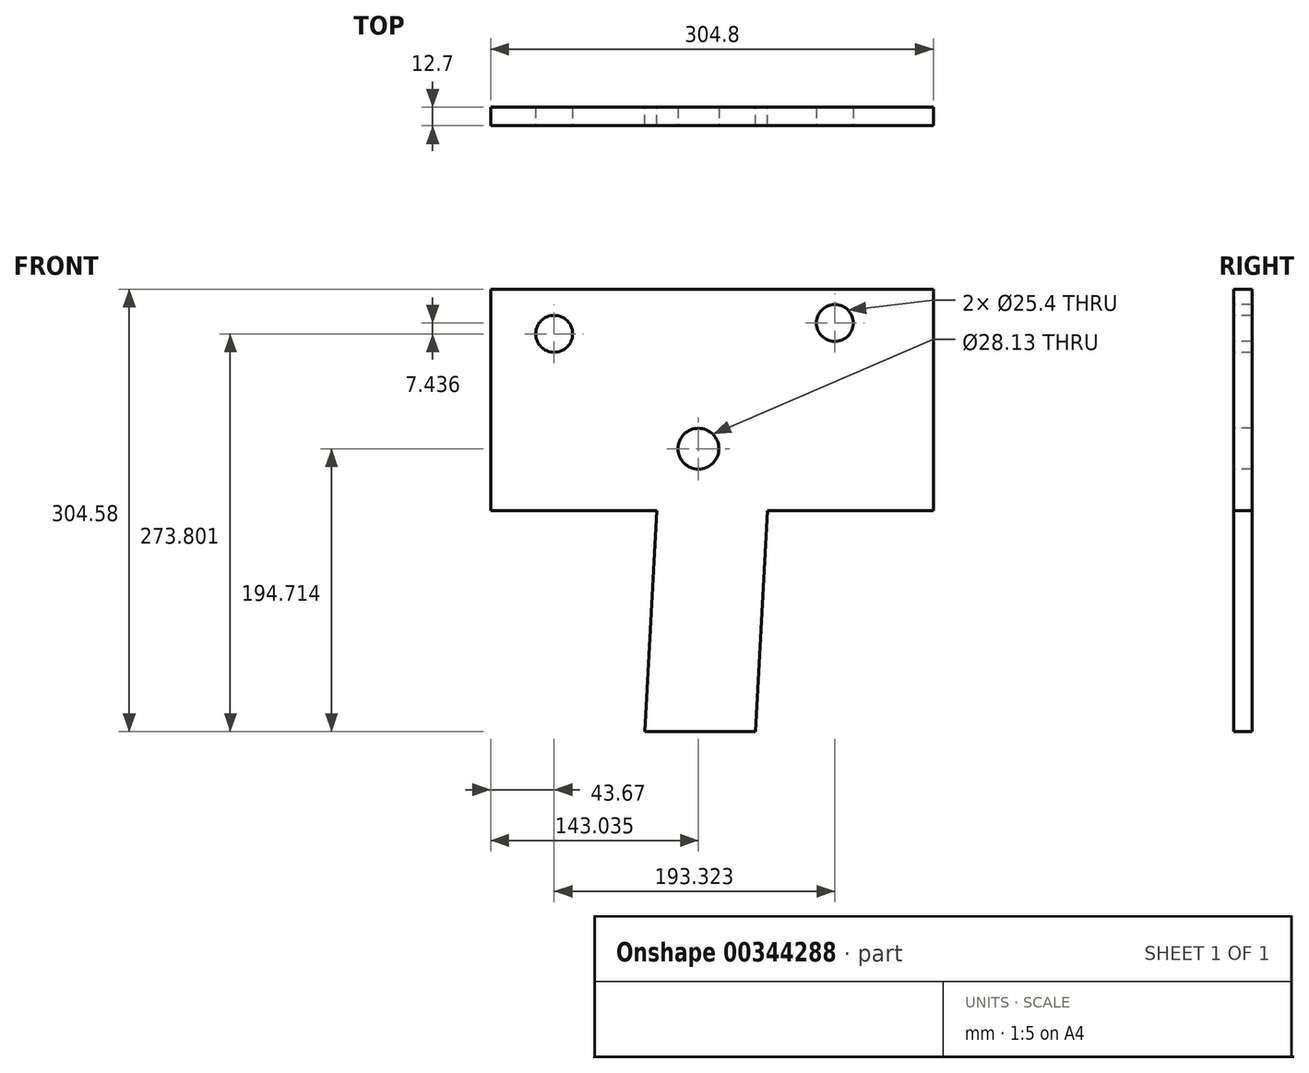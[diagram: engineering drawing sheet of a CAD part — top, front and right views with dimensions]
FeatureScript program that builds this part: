
annotation { "Feature Type Name" : "Feature", "Feature Type Description" : "" }
export const myFeature = defineFeature(function(context is Context, id is Id, definition is map)
    precondition{}
    {
        {
            var Q0;
            Q0=qCreatedBy(makeId("Front.planeOp"),FACE);
            var sketch = newSketch(context, id + "F0", { "sketchPlane" : qUnion([Q0])});
            skLineSegment(sketch, "E0", {"start": v(36.7, 42.76) * mm, "end": v(28.59, -109.42) * mm});
            skLineSegment(sketch, "E1", {"start": v(28.59, -109.42) * mm, "end": v(104.79, -109.42) * mm});
            skLineSegment(sketch, "E2", {"start": v(104.79, -109.42) * mm, "end": v(112.9, 42.76) * mm});
            skLineSegment(sketch, "E3", {"start": v(112.9, 42.76) * mm, "end": v(227.2, 42.76) * mm});
            skLineSegment(sketch, "E4", {"start": v(227.2, 42.76) * mm, "end": v(227.2, 195.16) * mm});
            skLineSegment(sketch, "E5", {"start": v(227.2, 195.16) * mm, "end": v(-77.6, 195.16) * mm});
            skLineSegment(sketch, "E6", {"start": v(-77.6, 195.16) * mm, "end": v(-77.6, 42.76) * mm});
            skLineSegment(sketch, "E7", {"start": v(-77.6, 42.76) * mm, "end": v(36.7, 42.76) * mm});
            skSolve(sketch);
        }
        {
            var Q0;
            Q0=makeQuery(id+"F0.imprint","IMPRINT",FACE,{"disambiguationData":[TD([[makeQuery(id+"F0.imprint","IMPRINT",EDGE,{"derivedFrom":sQuery(id+"F0.wireOp",EDGE,"E0")}),1.0]])]});
            extrude(context, id + "F1", {"entities" : qUnion([Q0]), "depth" : 12.7 * mm});
        }
        {
            var Q0;
            Q0=makeQuery(id+"F1.opExtrude","CAP_FACE",FACE,{"disambiguationData":[OSD([sQuery(id+"F0.wireOp",EDGE,"E0"),sQuery(id+"F0.wireOp",EDGE,"E1"),sQuery(id+"F0.wireOp",EDGE,"E2"),sQuery(id+"F0.wireOp",EDGE,"E3"),sQuery(id+"F0.wireOp",EDGE,"E4"),sQuery(id+"F0.wireOp",EDGE,"E5"),sQuery(id+"F0.wireOp",EDGE,"E6"),sQuery(id+"F0.wireOp",EDGE,"E7")])],"isStart":false});
            var sketch = newSketch(context, id + "F2", { "sketchPlane" : qUnion([Q0])});
            skCircle(sketch, "E8", {"center": v(-33.93, 164.38) * mm, "radius": 12.7 * mm});
            skCircle(sketch, "E9", {"center": v(159.4, 171.82) * mm, "radius": 12.7 * mm});
            skCircle(sketch, "E10", {"center": v(65.44, 85.3) * mm, "radius": 14.07 * mm});
            skSolve(sketch);
        }
        {
            var Q0;
            Q0=makeQuery(id+"F2.imprint","IMPRINT",FACE,{"disambiguationData":[TD([[makeQuery(id+"F2.imprint","IMPRINT",EDGE,{"derivedFrom":sQuery(id+"F2.wireOp",EDGE,"E8")}),1.0]])]});
            var Q1;
            Q1=makeQuery(id+"F2.imprint","IMPRINT",FACE,{"disambiguationData":[TD([[makeQuery(id+"F2.imprint","IMPRINT",EDGE,{"derivedFrom":sQuery(id+"F2.wireOp",EDGE,"E10")}),1.0]])]});
            var Q2;
            Q2=makeQuery(id+"F2.imprint","IMPRINT",FACE,{"disambiguationData":[TD([[makeQuery(id+"F2.imprint","IMPRINT",EDGE,{"derivedFrom":sQuery(id+"F2.wireOp",EDGE,"E9")}),1.0]])]});
            extrude(context, id + "F3", {"entities" : qUnion([Q0, Q1, Q2]), "operationType" : NewBodyOperationType.REMOVE, "oppositeDirection" : true, "depth" : 61.2 * mm});
        }
    });
